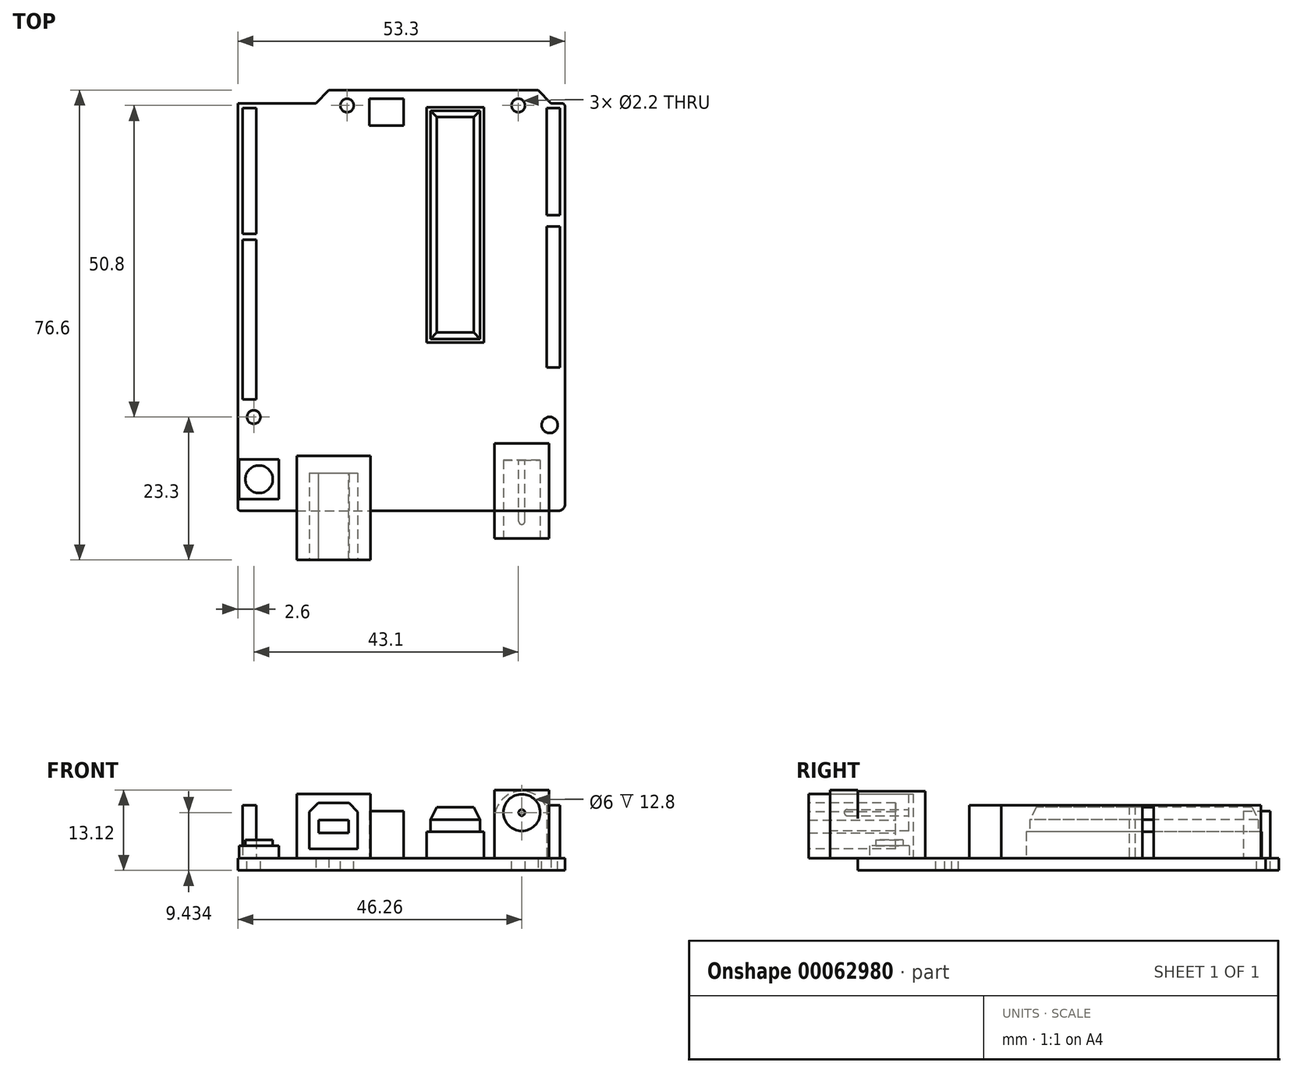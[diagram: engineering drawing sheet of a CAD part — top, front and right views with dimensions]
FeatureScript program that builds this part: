
annotation { "Feature Type Name" : "Feature", "Feature Type Description" : "" }
export const myFeature = defineFeature(function(context is Context, id is Id, definition is map)
    precondition{}
    {
        {
            var Q0;
            Q0=qCreatedBy(makeId("Top.planeOp"),FACE);
            var sketch = newSketch(context, id + "F0", { "sketchPlane" : qUnion([Q0])});
            skLineSegment(sketch, "E0.rect.bottom", {"start": v(-11.81, 34.3) * mm, "end": v(22.25, 34.3) * mm});
            skLineSegment(sketch, "E0.rect.top", {"start": v(-26.11, -34.3) * mm, "end": v(25.53, -34.3) * mm});
            skLineSegment(sketch, "E0.rect.left", {"start": v(-26.65, 32.16) * mm, "end": v(-26.65, -33.76) * mm});
            skLineSegment(sketch, "E0.rect.right", {"start": v(26.65, 31.62) * mm, "end": v(26.65, -33.18) * mm});
            skPoint(sketch, "E0.rect.middle", {"position": v(0, 0) * mm});
            skLineSegment(sketch, "E1.top", {"start": v(-25.49, 32.16) * mm, "end": v(-13.95, 32.16) * mm});
            skPoint(sketch, "E2.orphan", {"position": v(-26.65, 34.3) * mm});
            skLineSegment(sketch, "E3", {"start": v(-26.65, 32.16) * mm, "end": v(-25.49, 32.16) * mm});
            skLineSegment(sketch, "E4", {"start": v(-11.81, 34.3) * mm, "end": v(-13.95, 32.16) * mm});
            skLineSegment(sketch, "E5.top", {"start": v(24.39, 32.16) * mm, "end": v(26.11, 32.16) * mm});
            skLineSegment(sketch, "E6", {"start": v(22.25, 34.3) * mm, "end": v(24.39, 32.16) * mm});
            skPoint(sketch, "E7.orphan", {"position": v(26.65, 34.3) * mm});
            skPoint(sketch, "E8.visualSharp", {"position": v(26.65, -34.3) * mm});
            skArc(sketch, "E8.filletArc", {"start": v(25.53, -34.3) * mm, "mid": v(26.32, -33.97) * mm, "end": v(26.65, -33.18) * mm});
            skPoint(sketch, "E9.visualSharp", {"position": v(26.65, 32.16) * mm});
            skArc(sketch, "E9.filletArc", {"start": v(26.65, 31.62) * mm, "mid": v(26.5, 32) * mm, "end": v(26.11, 32.16) * mm});
            skPoint(sketch, "E10.visualSharp", {"position": v(-26.65, -34.3) * mm});
            skArc(sketch, "E10.filletArc", {"start": v(-26.65, -33.76) * mm, "mid": v(-26.5, -34.14) * mm, "end": v(-26.11, -34.3) * mm});
            skPoint(sketch, "E11.second.point", {"position": v(21.12, -10.57) * mm});
            skPoint(sketch, "E11.third.point", {"position": v(22.07, -8.93) * mm});
            skLineSegment(sketch, "E12", {"start": v(-13.95, 32.16) * mm, "end": v(31.22, 32.16) * mm, "construction": true});
            skSolve(sketch);
        }
        {
            var Q0;
            Q0=makeQuery(id+"F0.imprint","IMPRINT",FACE,{"disambiguationData":[TD([[makeQuery(id+"F0.imprint","IMPRINT",EDGE,{"derivedFrom":sQuery(id+"F0.wireOp",EDGE,"E0.rect.bottom")}),-1.0]])]});
            extrude(context, id + "F1", {"entities" : qUnion([Q0]), "depth" : 1.69 * mm});
        }
        {
            var Q0;
            Q0=makeQuery(id+"F1.opExtrude","CAP_FACE",FACE,{"disambiguationData":[OSD([sQuery(id+"F0.wireOp",EDGE,"E0.rect.bottom"),sQuery(id+"F0.wireOp",EDGE,"E0.rect.top"),sQuery(id+"F0.wireOp",EDGE,"E0.rect.left"),sQuery(id+"F0.wireOp",EDGE,"E0.rect.right"),sQuery(id+"F0.wireOp",EDGE,"E1.top"),sQuery(id+"F0.wireOp",EDGE,"E3"),sQuery(id+"F0.wireOp",EDGE,"E4"),sQuery(id+"F0.wireOp",EDGE,"E5.top"),sQuery(id+"F0.wireOp",EDGE,"E6"),sQuery(id+"F0.wireOp",EDGE,"E8.filletArc"),sQuery(id+"F0.wireOp",EDGE,"E9.filletArc"),sQuery(id+"F0.wireOp",EDGE,"E10.filletArc")])],"isStart":false});
            var sketch = newSketch(context, id + "F2", { "sketchPlane" : qUnion([Q0])});
            skLineSegment(sketch, "E13.top", {"start": v(23.65, -10.91) * mm, "end": v(25.85, -10.91) * mm});
            skLineSegment(sketch, "E13.left", {"start": v(23.65, 31.36) * mm, "end": v(23.65, 13.89) * mm});
            skLineSegment(sketch, "E13.right", {"start": v(25.85, 31.36) * mm, "end": v(25.85, 13.89) * mm});
            skLineSegment(sketch, "E14", {"start": v(23.65, 31.36) * mm, "end": v(25.85, 31.36) * mm});
            skLineSegment(sketch, "E15", {"start": v(23.65, 13.89) * mm, "end": v(25.85, 13.89) * mm});
            skLineSegment(sketch, "E16", {"start": v(23.65, 12.09) * mm, "end": v(25.85, 12.09) * mm});
            skLineSegment(sketch, "E17.trimOffspring", {"start": v(23.65, 12.09) * mm, "end": v(23.65, -10.91) * mm});
            skLineSegment(sketch, "E18.trimOffspring", {"start": v(25.85, 12.09) * mm, "end": v(25.85, -10.91) * mm});
            skLineSegment(sketch, "E19.bottom", {"start": v(-25.85, 31.36) * mm, "end": v(-23.65, 31.36) * mm});
            skLineSegment(sketch, "E19.top", {"start": v(-25.85, -16.12) * mm, "end": v(-23.65, -16.12) * mm});
            skLineSegment(sketch, "E19.left", {"start": v(-25.85, 31.36) * mm, "end": v(-25.85, 10.88) * mm});
            skLineSegment(sketch, "E19.right", {"start": v(-23.65, 31.36) * mm, "end": v(-23.65, 10.88) * mm});
            skLineSegment(sketch, "E20.bottom", {"start": v(-25.85, 10.88) * mm, "end": v(-23.65, 10.88) * mm});
            skLineSegment(sketch, "E20.top", {"start": v(-25.85, 9.88) * mm, "end": v(-23.65, 9.88) * mm});
            skLineSegment(sketch, "E21.trimOffspring", {"start": v(-23.65, 9.88) * mm, "end": v(-23.65, -16.12) * mm});
            skLineSegment(sketch, "E22.trimOffspring", {"start": v(-25.85, 9.88) * mm, "end": v(-25.85, -16.12) * mm});
            skSolve(sketch);
        }
        {
            var Q0;
            Q0=makeQuery(id+"F2.imprint","IMPRINT",FACE,{"disambiguationData":[TD([[makeQuery(id+"F2.imprint","IMPRINT",EDGE,{"derivedFrom":sQuery(id+"F2.wireOp",EDGE,"E13.top")}),1.0]])]});
            var Q1;
            Q1=makeQuery(id+"F2.imprint","IMPRINT",FACE,{"disambiguationData":[TD([[makeQuery(id+"F2.imprint","IMPRINT",EDGE,{"derivedFrom":sQuery(id+"F2.wireOp",EDGE,"E13.left")}),1.0]])]});
            var Q2;
            Q2=makeQuery(id+"F2.imprint","IMPRINT",FACE,{"disambiguationData":[TD([[makeQuery(id+"F2.imprint","IMPRINT",EDGE,{"derivedFrom":sQuery(id+"F2.wireOp",EDGE,"E19.bottom")}),-1.0]])]});
            var Q3;
            Q3=makeQuery(id+"F2.imprint","IMPRINT",FACE,{"disambiguationData":[TD([[makeQuery(id+"F2.imprint","IMPRINT",EDGE,{"derivedFrom":sQuery(id+"F2.wireOp",EDGE,"E19.top")}),1.0]])]});
            extrude(context, id + "F3", {"entities" : qUnion([Q0, Q1, Q2, Q3]), "depth" : 8.6 * mm});
        }
        {
            var Q0;
            Q0=makeQuery(id+"F1.opExtrude","SWEPT_FACE",FACE,{"disambiguationData":[OSD([sQuery(id+"F0.wireOp",EDGE,"E0.rect.top")])]});
            cPlane(context, id + "F4", {"entities" : qUnion([Q0]), "cplaneType" : CPlaneType.OFFSET, "offset" : 0 * mm, "width" : 150 * mm, "height" : 150 * mm});
        }
        {
            var Q0;
            Q0=qCreatedBy(id+"F4.planeOp",FACE);
            var sketch = newSketch(context, id + "F5", { "sketchPlane" : qUnion([Q0])});
            skLineSegment(sketch, "E23", {"start": v(32.01, 1.68) * mm, "end": v(24.05, 1.68) * mm, "construction": true});
            skLineSegment(sketch, "E24.bottom", {"start": v(24.05, 1.68) * mm, "end": v(15.17, 1.68) * mm});
            skLineSegment(sketch, "E24.left", {"start": v(24.05, 1.68) * mm, "end": v(24.05, 8.18) * mm});
            skLineSegment(sketch, "E24.right", {"start": v(15.17, 1.68) * mm, "end": v(15.17, 8.18) * mm});
            skArc(sketch, "E25", {"start": v(24.05, 8.18) * mm, "mid": v(19.6, 12.62) * mm, "end": v(15.17, 8.18) * mm});
            skSolve(sketch);
        }
        {
            var Q0;
            Q0=makeQuery(id+"F5.imprint","IMPRINT",FACE,{"disambiguationData":[TD([[makeQuery(id+"F5.imprint","IMPRINT",EDGE,{"derivedFrom":sQuery(id+"F5.wireOp",EDGE,"E24.bottom")}),-1.0]])]});
            extrude(context, id + "F6", {"entities" : qUnion([Q0]), "oppositeDirection" : true, "depth" : 11 * mm});
        }
        {
            var Q0;
            Q0=qCreatedBy(id+"F4.planeOp",FACE);
            var sketch = newSketch(context, id + "F7", { "sketchPlane" : qUnion([Q0])});
            skLineSegment(sketch, "E26.bottom", {"start": v(15.17, 1.69) * mm, "end": v(24.05, 1.69) * mm});
            skLineSegment(sketch, "E26.top", {"start": v(15.17, 12.81) * mm, "end": v(24.05, 12.81) * mm});
            skLineSegment(sketch, "E26.left", {"start": v(15.17, 1.69) * mm, "end": v(15.17, 12.81) * mm});
            skLineSegment(sketch, "E26.right", {"start": v(24.05, 1.69) * mm, "end": v(24.05, 12.81) * mm});
            skSolve(sketch);
        }
        {
            var Q0;
            Q0=makeQuery(id+"F7.imprint","IMPRINT",FACE,{"disambiguationData":[TD([[makeQuery(id+"F7.imprint","IMPRINT",EDGE,{"derivedFrom":sQuery(id+"F7.wireOp",EDGE,"E26.bottom")}),1.0]])]});
            extrude(context, id + "F8", {"entities" : qUnion([Q0]), "operationType" : NewBodyOperationType.ADD, "depth" : 4.5 * mm});
        }
        {
            var Q0;
            Q0=makeQuery(id+"F8.opExtrude","CAP_FACE",FACE,{"disambiguationData":[OSD([sQuery(id+"F7.wireOp",EDGE,"E26.bottom"),sQuery(id+"F7.wireOp",EDGE,"E26.top"),sQuery(id+"F7.wireOp",EDGE,"E26.left"),sQuery(id+"F7.wireOp",EDGE,"E26.right")])],"isStart":false});
            var sketch = newSketch(context, id + "F9", { "sketchPlane" : qUnion([Q0])});
            skCircle(sketch, "E27", {"center": v(19.6, 9.12) * mm, "radius": 3 * mm});
            skSolve(sketch);
        }
        {
            var Q0;
            Q0=makeQuery(id+"F9.imprint","IMPRINT",FACE,{"disambiguationData":[TD([[makeQuery(id+"F9.imprint","IMPRINT",EDGE,{"derivedFrom":sQuery(id+"F9.wireOp",EDGE,"E27")}),1.0]])]});
            var Q1;
            Q1=sQuery(id+"F9.wireOp",EDGE,"E27");
            extrude(context, id + "F10", {"entities" : qUnion([Q0]), "operationType" : NewBodyOperationType.REMOVE, "surfaceEntities" : qUnion([Q1]), "oppositeDirection" : true, "depth" : 12.8 * mm});
        }
        {
            var Q0;
            Q0=makeQuery(id+"F10.boolean.opBoolean","COPY",FACE,{"derivedFrom":makeQuery(id+"F10.opExtrude","CAP_FACE",FACE,{"disambiguationData":[OSD([sQuery(id+"F9.wireOp",EDGE,"E27")])],"isStart":false})});
            var sketch = newSketch(context, id + "F11", { "sketchPlane" : qUnion([Q0])});
            skCircle(sketch, "E28.0", {"center": v(19.6, 9.12) * mm, "radius": 3 * mm});
            skCircle(sketch, "E29", {"center": v(19.6, 9.12) * mm, "radius": 0.5 * mm});
            skSolve(sketch);
        }
        {
            var Q0;
            Q0=makeQuery(id+"F11.imprint","IMPRINT",FACE,{"disambiguationData":[TD([[makeQuery(id+"F11.imprint","IMPRINT",EDGE,{"derivedFrom":sQuery(id+"F11.wireOp",EDGE,"E29")}),1.0]])]});
            var Q1;
            Q1=sQuery(id+"F11.wireOp",EDGE,"E29");
            extrude(context, id + "F12", {"entities" : qUnion([Q0]), "surfaceEntities" : qUnion([Q1]), "depth" : 10 * mm});
        }
        {
            var Q0;
            Q0=makeQuery(id+"F1.opExtrude","CAP_FACE",FACE,{"disambiguationData":[OSD([sQuery(id+"F0.wireOp",EDGE,"E0.rect.bottom"),sQuery(id+"F0.wireOp",EDGE,"E0.rect.top"),sQuery(id+"F0.wireOp",EDGE,"E0.rect.left"),sQuery(id+"F0.wireOp",EDGE,"E0.rect.right"),sQuery(id+"F0.wireOp",EDGE,"E1.top"),sQuery(id+"F0.wireOp",EDGE,"E3"),sQuery(id+"F0.wireOp",EDGE,"E4"),sQuery(id+"F0.wireOp",EDGE,"E5.top"),sQuery(id+"F0.wireOp",EDGE,"E6"),sQuery(id+"F0.wireOp",EDGE,"E8.filletArc"),sQuery(id+"F0.wireOp",EDGE,"E9.filletArc"),sQuery(id+"F0.wireOp",EDGE,"E10.filletArc")])],"isStart":false});
            var sketch = newSketch(context, id + "F13", { "sketchPlane" : qUnion([Q0])});
            skLineSegment(sketch, "E30.bottom", {"start": v(-17.05, -34.3) * mm, "end": v(-5.05, -34.3) * mm});
            skLineSegment(sketch, "E30.top", {"start": v(-17.05, -25.3) * mm, "end": v(-5.05, -25.3) * mm});
            skLineSegment(sketch, "E30.left", {"start": v(-17.05, -34.3) * mm, "end": v(-17.05, -25.3) * mm});
            skLineSegment(sketch, "E30.right", {"start": v(-5.05, -34.3) * mm, "end": v(-5.05, -25.3) * mm});
            skSolve(sketch);
        }
        {
            var Q0;
            Q0=makeQuery(id+"F13.imprint","IMPRINT",FACE,{"disambiguationData":[TD([[makeQuery(id+"F13.imprint","IMPRINT",EDGE,{"derivedFrom":sQuery(id+"F13.wireOp",EDGE,"E30.bottom")}),1.0]])]});
            extrude(context, id + "F14", {"entities" : qUnion([Q0]), "depth" : 10.5 * mm});
        }
        {
            var Q0;
            Q0=makeQuery(id+"F14.opExtrude","SWEPT_FACE",FACE,{"disambiguationData":[OSD([sQuery(id+"F13.wireOp",EDGE,"E30.bottom")])]});
            var sketch = newSketch(context, id + "F15", { "sketchPlane" : qUnion([Q0])});
            skLineSegment(sketch, "E31.bottom", {"start": v(-17.05, 12.2) * mm, "end": v(-5.05, 12.2) * mm});
            skLineSegment(sketch, "E31.top", {"start": v(-17.05, 1.69) * mm, "end": v(-5.05, 1.69) * mm});
            skLineSegment(sketch, "E31.left", {"start": v(-17.05, 12.2) * mm, "end": v(-17.05, 1.69) * mm});
            skLineSegment(sketch, "E31.right", {"start": v(-5.05, 12.2) * mm, "end": v(-5.05, 1.69) * mm});
            skSolve(sketch);
        }
        {
            var Q0;
            Q0=makeQuery(id+"F15.imprint","IMPRINT",FACE,{"disambiguationData":[TD([[makeQuery(id+"F15.imprint","IMPRINT",EDGE,{"derivedFrom":sQuery(id+"F15.wireOp",EDGE,"E31.bottom")}),-1.0]])]});
            extrude(context, id + "F16", {"entities" : qUnion([Q0]), "operationType" : NewBodyOperationType.ADD, "depth" : 8 * mm});
        }
        {
            var Q0;
            Q0=makeQuery(id+"F16.opExtrude","CAP_FACE",FACE,{"disambiguationData":[OSD([sQuery(id+"F15.wireOp",EDGE,"E31.bottom"),sQuery(id+"F15.wireOp",EDGE,"E31.top"),sQuery(id+"F15.wireOp",EDGE,"E31.left"),sQuery(id+"F15.wireOp",EDGE,"E31.right")])],"isStart":false});
            var sketch = newSketch(context, id + "F17", { "sketchPlane" : qUnion([Q0])});
            skLineSegment(sketch, "E32.rect.bottom", {"start": v(-15, 3.2) * mm, "end": v(-7.1, 3.2) * mm});
            skLineSegment(sketch, "E32.rect.top", {"start": v(-13.56, 10.7) * mm, "end": v(-8.54, 10.7) * mm});
            skLineSegment(sketch, "E32.rect.left", {"start": v(-15, 3.2) * mm, "end": v(-15, 9.25) * mm});
            skLineSegment(sketch, "E32.rect.right", {"start": v(-7.1, 3.2) * mm, "end": v(-7.1, 9.25) * mm});
            skPoint(sketch, "E32.rect.middle", {"position": v(-11.05, 6.94) * mm});
            skPoint(sketch, "E32.rect.middle.positionSnap0", {"position": v(-17.05, 6.94) * mm});
            skPoint(sketch, "E32.rect.middle.positionSnap1", {"position": v(-11.05, 12.2) * mm});
            skPoint(sketch, "E32.rect.centerSnap0", {"position": v(-17.05, 6.94) * mm});
            skPoint(sketch, "E32.rect.centerSnap1", {"position": v(-11.05, 12.2) * mm});
            skLineSegment(sketch, "E33", {"start": v(-15, 9.25) * mm, "end": v(-13.56, 10.7) * mm});
            skLineSegment(sketch, "E34", {"start": v(-8.54, 10.7) * mm, "end": v(-7.1, 9.25) * mm});
            skPoint(sketch, "E35.orphan", {"position": v(-15, 10.7) * mm});
            skPoint(sketch, "E36.orphan", {"position": v(-7.1, 10.7) * mm});
            skSolve(sketch);
        }
        {
            var Q0;
            Q0=makeQuery(id+"F17.imprint","IMPRINT",FACE,{"disambiguationData":[TD([[makeQuery(id+"F17.imprint","IMPRINT",EDGE,{"derivedFrom":sQuery(id+"F17.wireOp",EDGE,"E32.rect.bottom")}),1.0]])]});
            extrude(context, id + "F18", {"entities" : qUnion([Q0]), "operationType" : NewBodyOperationType.REMOVE, "oppositeDirection" : true, "depth" : 14.14 * mm});
        }
        {
            var Q0;
            Q0=makeQuery(id+"F18.boolean.opBoolean","COPY",FACE,{"derivedFrom":makeQuery(id+"F18.opExtrude","CAP_FACE",FACE,{"disambiguationData":[OSD([sQuery(id+"F17.wireOp",EDGE,"E32.rect.bottom"),sQuery(id+"F17.wireOp",EDGE,"E32.rect.top"),sQuery(id+"F17.wireOp",EDGE,"E32.rect.left"),sQuery(id+"F17.wireOp",EDGE,"E32.rect.right"),sQuery(id+"F17.wireOp",EDGE,"E33"),sQuery(id+"F17.wireOp",EDGE,"E34")])],"isStart":false})});
            var sketch = newSketch(context, id + "F19", { "sketchPlane" : qUnion([Q0])});
            skLineSegment(sketch, "E37.rect.bottom", {"start": v(-13.49, 5.84) * mm, "end": v(-8.6, 5.84) * mm});
            skLineSegment(sketch, "E37.rect.top", {"start": v(-13.49, 7.92) * mm, "end": v(-8.6, 7.92) * mm});
            skLineSegment(sketch, "E37.rect.left", {"start": v(-13.49, 5.84) * mm, "end": v(-13.49, 7.92) * mm});
            skLineSegment(sketch, "E37.rect.right", {"start": v(-8.6, 5.84) * mm, "end": v(-8.6, 7.92) * mm});
            skPoint(sketch, "E37.rect.middle", {"position": v(-11.05, 6.88) * mm});
            skPoint(sketch, "E37.rect.middle.positionSnap0", {"position": v(-11.05, 10.7) * mm});
            skPoint(sketch, "E37.rect.centerSnap0", {"position": v(-11.05, 10.7) * mm});
            skSolve(sketch);
        }
        {
            var Q0;
            Q0=qSketchRegion(id+"F19",true);
            var Q1;
            Q1=makeQuery(id+"F16.opExtrude","CAP_FACE",FACE,{"disambiguationData":[OSD([sQuery(id+"F15.wireOp",EDGE,"E31.bottom"),sQuery(id+"F15.wireOp",EDGE,"E31.top"),sQuery(id+"F15.wireOp",EDGE,"E31.left"),sQuery(id+"F15.wireOp",EDGE,"E31.right")])],"isStart":false});
            extrude(context, id + "F20", {"entities" : qUnion([Q0]), "endBound" : BoundingType.UP_TO_SURFACE, "endBoundEntityFace" : qUnion([Q1]), "depth" : 25 * mm});
        }
        {
            var Q0;
            Q0=makeQuery(id+"F1.opExtrude","CAP_FACE",FACE,{"disambiguationData":[OSD([sQuery(id+"F0.wireOp",EDGE,"E0.rect.bottom"),sQuery(id+"F0.wireOp",EDGE,"E0.rect.top"),sQuery(id+"F0.wireOp",EDGE,"E0.rect.left"),sQuery(id+"F0.wireOp",EDGE,"E0.rect.right"),sQuery(id+"F0.wireOp",EDGE,"E1.top"),sQuery(id+"F0.wireOp",EDGE,"E3"),sQuery(id+"F0.wireOp",EDGE,"E4"),sQuery(id+"F0.wireOp",EDGE,"E5.top"),sQuery(id+"F0.wireOp",EDGE,"E6"),sQuery(id+"F0.wireOp",EDGE,"E8.filletArc"),sQuery(id+"F0.wireOp",EDGE,"E9.filletArc"),sQuery(id+"F0.wireOp",EDGE,"E10.filletArc")])],"isStart":false});
            var sketch = newSketch(context, id + "F21", { "sketchPlane" : qUnion([Q0])});
            skLineSegment(sketch, "E38.rect.bottom", {"start": v(-26.44, -25.9) * mm, "end": v(-19.94, -25.9) * mm});
            skLineSegment(sketch, "E38.rect.top", {"start": v(-26.44, -32.4) * mm, "end": v(-19.94, -32.4) * mm});
            skLineSegment(sketch, "E38.rect.left", {"start": v(-26.44, -25.9) * mm, "end": v(-26.44, -32.4) * mm});
            skLineSegment(sketch, "E38.rect.right", {"start": v(-19.94, -25.9) * mm, "end": v(-19.94, -32.4) * mm});
            skPoint(sketch, "E38.rect.middle", {"position": v(-23.19, -29.14) * mm});
            skSolve(sketch);
        }
        {
            var Q0;
            Q0=makeQuery(id+"F21.imprint","IMPRINT",FACE,{"disambiguationData":[TD([[makeQuery(id+"F21.imprint","IMPRINT",EDGE,{"derivedFrom":sQuery(id+"F21.wireOp",EDGE,"E38.rect.bottom")}),-1.0]])]});
            extrude(context, id + "F22", {"entities" : qUnion([Q0]), "depth" : 2 * mm});
        }
        {
            var Q0;
            Q0=makeQuery(id+"F22.opExtrude","CAP_FACE",FACE,{"disambiguationData":[OSD([sQuery(id+"F21.wireOp",EDGE,"E38.rect.bottom"),sQuery(id+"F21.wireOp",EDGE,"E38.rect.top"),sQuery(id+"F21.wireOp",EDGE,"E38.rect.left"),sQuery(id+"F21.wireOp",EDGE,"E38.rect.right")])],"isStart":false});
            var sketch = newSketch(context, id + "F23", { "sketchPlane" : qUnion([Q0])});
            skCircle(sketch, "E39", {"center": v(-23.19, -29.14) * mm, "radius": 2.24 * mm});
            skPoint(sketch, "E39.centerSnap0", {"position": v(-26.44, -29.14) * mm});
            skSolve(sketch);
        }
        {
            var Q0;
            Q0=makeQuery(id+"F23.imprint","IMPRINT",FACE,{"disambiguationData":[TD([[makeQuery(id+"F23.imprint","IMPRINT",EDGE,{"derivedFrom":sQuery(id+"F23.wireOp",EDGE,"E39")}),1.0]])]});
            extrude(context, id + "F24", {"entities" : qUnion([Q0]), "depth" : 1 * mm});
        }
        {
            var Q0;
            Q0=makeQuery(id+"F1.opExtrude","CAP_FACE",FACE,{"disambiguationData":[OSD([sQuery(id+"F0.wireOp",EDGE,"E0.rect.bottom"),sQuery(id+"F0.wireOp",EDGE,"E0.rect.top"),sQuery(id+"F0.wireOp",EDGE,"E0.rect.left"),sQuery(id+"F0.wireOp",EDGE,"E0.rect.right"),sQuery(id+"F0.wireOp",EDGE,"E1.top"),sQuery(id+"F0.wireOp",EDGE,"E3"),sQuery(id+"F0.wireOp",EDGE,"E4"),sQuery(id+"F0.wireOp",EDGE,"E5.top"),sQuery(id+"F0.wireOp",EDGE,"E6"),sQuery(id+"F0.wireOp",EDGE,"E8.filletArc"),sQuery(id+"F0.wireOp",EDGE,"E9.filletArc"),sQuery(id+"F0.wireOp",EDGE,"E10.filletArc")])],"isStart":false});
            var sketch = newSketch(context, id + "F25", { "sketchPlane" : qUnion([Q0])});
            skLineSegment(sketch, "E40.bottom", {"start": v(13.47, 31.5) * mm, "end": v(4.14, 31.5) * mm});
            skLineSegment(sketch, "E40.top", {"start": v(13.47, -6.87) * mm, "end": v(4.14, -6.87) * mm});
            skLineSegment(sketch, "E40.left", {"start": v(13.47, 31.5) * mm, "end": v(13.47, -6.87) * mm});
            skLineSegment(sketch, "E40.right", {"start": v(4.14, 31.5) * mm, "end": v(4.14, -6.87) * mm});
            skSolve(sketch);
        }
        {
            var Q0;
            Q0=makeQuery(id+"F25.imprint","IMPRINT",FACE,{"disambiguationData":[TD([[makeQuery(id+"F25.imprint","IMPRINT",EDGE,{"derivedFrom":sQuery(id+"F25.wireOp",EDGE,"E40.bottom")}),1.0]])]});
            extrude(context, id + "F26", {"entities" : qUnion([Q0]), "depth" : 4.3 * mm});
        }
        {
            var Q0;
            Q0=makeQuery(id+"F26.opExtrude","CAP_FACE",FACE,{"disambiguationData":[OSD([sQuery(id+"F25.wireOp",EDGE,"E40.bottom"),sQuery(id+"F25.wireOp",EDGE,"E40.top"),sQuery(id+"F25.wireOp",EDGE,"E40.left"),sQuery(id+"F25.wireOp",EDGE,"E40.right")])],"isStart":false});
            var sketch = newSketch(context, id + "F27", { "sketchPlane" : qUnion([Q0])});
            skLineSegment(sketch, "E41.rect.bottom", {"start": v(4.76, 30.91) * mm, "end": v(12.84, 30.91) * mm});
            skLineSegment(sketch, "E41.rect.top", {"start": v(4.76, -6.28) * mm, "end": v(12.84, -6.28) * mm});
            skLineSegment(sketch, "E41.rect.left", {"start": v(4.76, 30.91) * mm, "end": v(4.76, -6.28) * mm});
            skLineSegment(sketch, "E41.rect.right", {"start": v(12.84, 30.91) * mm, "end": v(12.84, -6.28) * mm});
            skPoint(sketch, "E41.rect.middle", {"position": v(8.8, 12.32) * mm});
            skPoint(sketch, "E41.rect.middle.positionSnap0", {"position": v(8.8, 31.5) * mm});
            skPoint(sketch, "E41.rect.middle.positionSnap1", {"position": v(4.14, 12.32) * mm});
            skPoint(sketch, "E41.rect.centerSnap0", {"position": v(8.8, 31.5) * mm});
            skPoint(sketch, "E41.rect.centerSnap1", {"position": v(4.14, 12.32) * mm});
            skSolve(sketch);
        }
        {
            var Q0;
            Q0=makeQuery(id+"F27.imprint","IMPRINT",FACE,{"disambiguationData":[TD([[makeQuery(id+"F27.imprint","IMPRINT",EDGE,{"derivedFrom":sQuery(id+"F27.wireOp",EDGE,"E41.rect.bottom")}),-1.0]])]});
            extrude(context, id + "F28", {"entities" : qUnion([Q0]), "depth" : 2 * mm});
        }
        {
            var Q0;
            Q0=makeQuery(id+"F28.opExtrude","CAP_FACE",FACE,{"disambiguationData":[OSD([sQuery(id+"F27.wireOp",EDGE,"E41.rect.bottom"),sQuery(id+"F27.wireOp",EDGE,"E41.rect.top"),sQuery(id+"F27.wireOp",EDGE,"E41.rect.left"),sQuery(id+"F27.wireOp",EDGE,"E41.rect.right")])],"isStart":false});
            cPlane(context, id + "F29", {"entities" : qUnion([Q0]), "cplaneType" : CPlaneType.OFFSET, "offset" : 2 * mm, "width" : 150 * mm, "height" : 150 * mm});
        }
        {
            var Q0;
            Q0=qCreatedBy(id+"F29.planeOp",FACE);
            var sketch = newSketch(context, id + "F30", { "sketchPlane" : qUnion([Q0])});
            skLineSegment(sketch, "E42.bottom", {"start": v(5.78, 29.94) * mm, "end": v(11.83, 29.94) * mm});
            skLineSegment(sketch, "E42.top", {"start": v(5.78, -5.22) * mm, "end": v(11.83, -5.22) * mm});
            skLineSegment(sketch, "E42.left", {"start": v(5.78, 29.94) * mm, "end": v(5.78, -5.22) * mm});
            skLineSegment(sketch, "E42.right", {"start": v(11.83, 29.94) * mm, "end": v(11.83, -5.22) * mm});
            skSolve(sketch);
        }
        {
            var Q1;
            Q1=makeQuery(id+"F30.imprint","IMPRINT",FACE,{"disambiguationData":[TD([[makeQuery(id+"F30.imprint","IMPRINT",EDGE,{"derivedFrom":sQuery(id+"F30.wireOp",EDGE,"E42.bottom")}),-1.0]])]});
            var Q2;
            Q2=makeQuery(id+"F28.opExtrude","CAP_FACE",FACE,{"disambiguationData":[OSD([sQuery(id+"F27.wireOp",EDGE,"E41.rect.bottom"),sQuery(id+"F27.wireOp",EDGE,"E41.rect.top"),sQuery(id+"F27.wireOp",EDGE,"E41.rect.left"),sQuery(id+"F27.wireOp",EDGE,"E41.rect.right")])],"isStart":false});
            loft(context, id + "F31", {"sheetProfilesArray" : [{ "sheetProfileEntities" : qUnion([Q1]) }, { "sheetProfileEntities" : qUnion([Q2]) }]});
        }
        {
            var Q0;
            Q0=makeQuery(id+"F1.opExtrude","CAP_FACE",FACE,{"disambiguationData":[OSD([sQuery(id+"F0.wireOp",EDGE,"E0.rect.bottom"),sQuery(id+"F0.wireOp",EDGE,"E0.rect.top"),sQuery(id+"F0.wireOp",EDGE,"E0.rect.left"),sQuery(id+"F0.wireOp",EDGE,"E0.rect.right"),sQuery(id+"F0.wireOp",EDGE,"E1.top"),sQuery(id+"F0.wireOp",EDGE,"E3"),sQuery(id+"F0.wireOp",EDGE,"E4"),sQuery(id+"F0.wireOp",EDGE,"E5.top"),sQuery(id+"F0.wireOp",EDGE,"E6"),sQuery(id+"F0.wireOp",EDGE,"E8.filletArc"),sQuery(id+"F0.wireOp",EDGE,"E9.filletArc"),sQuery(id+"F0.wireOp",EDGE,"E10.filletArc")])],"isStart":false});
            var sketch = newSketch(context, id + "F32", { "sketchPlane" : qUnion([Q0])});
            skCircle(sketch, "E43", {"center": v(24.15, -20.3) * mm, "radius": 1.31 * mm});
            skLineSegment(sketch, "E44", {"start": v(24.15, -20.3) * mm, "end": v(-35.14, -20.3) * mm, "construction": true});
            skLineSegment(sketch, "E45.0", {"start": v(24.15, -19) * mm, "end": v(-35.14, -19) * mm, "construction": true});
            skCircle(sketch, "E46", {"center": v(-24.05, -19) * mm, "radius": 1.1 * mm});
            skSolve(sketch);
        }
        {
            var Q0;
            Q0=makeQuery(id+"F32.imprint","IMPRINT",FACE,{"disambiguationData":[TD([[makeQuery(id+"F32.imprint","IMPRINT",EDGE,{"derivedFrom":sQuery(id+"F32.wireOp",EDGE,"E46")}),1.0]])]});
            var Q1;
            Q1=makeQuery(id+"F32.imprint","IMPRINT",FACE,{"disambiguationData":[TD([[makeQuery(id+"F32.imprint","IMPRINT",EDGE,{"derivedFrom":sQuery(id+"F32.wireOp",EDGE,"E43")}),1.0]])]});
            var Q2;
            Q2=sQuery(id+"F32.wireOp",EDGE,"07041a57-2a46-4494-bb32-0d5364b2cb77");
            var Q3;
            Q3=sQuery(id+"F32.wireOp",EDGE,"E43");
            extrude(context, id + "F33", {"entities" : qUnion([Q0, Q1]), "operationType" : NewBodyOperationType.REMOVE, "surfaceEntities" : qUnion([Q2, Q3]), "endBound" : BoundingType.THROUGH_ALL, "oppositeDirection" : true, "depth" : 25 * mm});
        }
        {
            var Q0;
            Q0=makeQuery(id+"F12.opExtrude","CAP_FACE",FACE,{"disambiguationData":[OSD([sQuery(id+"F11.wireOp",EDGE,"E29")])],"isStart":false});
            var sketch = newSketch(context, id + "F34", { "sketchPlane" : qUnion([Q0])});
            skArc(sketch, "E47.0", {"start": v(19.6, 9.62) * mm, "mid": v(19.1, 9.12) * mm, "end": v(19.6, 8.62) * mm});
            skLineSegment(sketch, "E48", {"start": v(19.6, 9.62) * mm, "end": v(19.6, 8.62) * mm});
            skSolve(sketch);
        }
        {
            var Q0;
            {var subQ2=sQuery(id+"F34.wireOp",EDGE,"E48");Q0=makeQuery(id+"F34.imprint","IMPRINT",FACE,{"disambiguationData":[TD([[makeQuery(id+"F34.imprint","IMPRINT",EDGE,{"derivedFrom":subQ2}),1.0]])]});}
            var Q1;
            Q1=sQuery(id+"F34.wireOp",EDGE,"E48");
            revolve(context, id + "F35", {"operationType" : NewBodyOperationType.ADD, "entities" : qUnion([Q0]), "axis" : qUnion([Q1]), "revolveType" : RevolveType.ONE_DIRECTION, "angle" : 180 * degree});
        }
        {
            var Q0;
            Q0=makeQuery(id+"F1.opExtrude","CAP_FACE",FACE,{"disambiguationData":[OSD([sQuery(id+"F0.wireOp",EDGE,"E0.rect.bottom"),sQuery(id+"F0.wireOp",EDGE,"E0.rect.top"),sQuery(id+"F0.wireOp",EDGE,"E0.rect.left"),sQuery(id+"F0.wireOp",EDGE,"E0.rect.right"),sQuery(id+"F0.wireOp",EDGE,"E1.top"),sQuery(id+"F0.wireOp",EDGE,"E3"),sQuery(id+"F0.wireOp",EDGE,"E4"),sQuery(id+"F0.wireOp",EDGE,"E5.top"),sQuery(id+"F0.wireOp",EDGE,"E6"),sQuery(id+"F0.wireOp",EDGE,"E8.filletArc"),sQuery(id+"F0.wireOp",EDGE,"E9.filletArc"),sQuery(id+"F0.wireOp",EDGE,"E10.filletArc")])],"isStart":false});
            var sketch = newSketch(context, id + "F36", { "sketchPlane" : qUnion([Q0])});
            skCircle(sketch, "E49", {"center": v(-8.85, 31.8) * mm, "radius": 1.1 * mm});
            skCircle(sketch, "E50", {"center": v(19.05, 31.8) * mm, "radius": 1.1 * mm});
            skCircle(sketch, "E51.0", {"center": v(24.15, -20.3) * mm, "radius": 1.31 * mm, "construction": true});
            skCircle(sketch, "E52.0", {"center": v(-24.05, -19) * mm, "radius": 1.1 * mm});
            skSolve(sketch);
        }
        {
            var Q0;
            Q0 = qSketchRegion(id + "F36", true);
            extrude(context, id + "F37", {"entities" : qUnion([Q0]), "operationType" : NewBodyOperationType.REMOVE, "oppositeDirection" : true, "depth" : 25 * mm});
        }
        {
            var Q0;
            Q0=makeQuery(id+"F1.opExtrude","CAP_FACE",FACE,{"disambiguationData":[OSD([sQuery(id+"F0.wireOp",EDGE,"E0.rect.bottom"),sQuery(id+"F0.wireOp",EDGE,"E0.rect.top"),sQuery(id+"F0.wireOp",EDGE,"E0.rect.left"),sQuery(id+"F0.wireOp",EDGE,"E0.rect.right"),sQuery(id+"F0.wireOp",EDGE,"E1.top"),sQuery(id+"F0.wireOp",EDGE,"E3"),sQuery(id+"F0.wireOp",EDGE,"E4"),sQuery(id+"F0.wireOp",EDGE,"E5.top"),sQuery(id+"F0.wireOp",EDGE,"E6"),sQuery(id+"F0.wireOp",EDGE,"E8.filletArc"),sQuery(id+"F0.wireOp",EDGE,"E9.filletArc"),sQuery(id+"F0.wireOp",EDGE,"E10.filletArc")])],"isStart":false});
            var sketch = newSketch(context, id + "F38", { "sketchPlane" : qUnion([Q0])});
            skLineSegment(sketch, "E53.0", {"start": v(26.65, 31.62) * mm, "end": v(26.65, -33.18) * mm});
            skLineSegment(sketch, "E54.0", {"start": v(-26.11, -34.3) * mm, "end": v(25.53, -34.3) * mm});
            skLineSegment(sketch, "E55.0", {"start": v(-26.65, 32.16) * mm, "end": v(-26.65, -33.76) * mm});
            skLineSegment(sketch, "E56.0", {"start": v(-26.65, 32.16) * mm, "end": v(-13.95, 32.16) * mm});
            skLineSegment(sketch, "E57.0", {"start": v(-11.81, 34.3) * mm, "end": v(22.25, 34.3) * mm});
            skCircle(sketch, "E58.0", {"center": v(19.05, 31.8) * mm, "radius": 1.1 * mm});
            skCircle(sketch, "E59.0", {"center": v(-8.85, 31.8) * mm, "radius": 1.1 * mm});
            skCircle(sketch, "E60.0", {"center": v(-24.05, -19) * mm, "radius": 1.1 * mm});
            skCircle(sketch, "E61.0", {"center": v(24.15, -20.3) * mm, "radius": 1.31 * mm});
            skLineSegment(sketch, "E62.0", {"start": v(-11.81, 34.3) * mm, "end": v(-13.95, 32.16) * mm});
            skLineSegment(sketch, "E63.0", {"start": v(22.25, 34.3) * mm, "end": v(24.39, 32.16) * mm});
            skLineSegment(sketch, "E64.0", {"start": v(24.39, 32.16) * mm, "end": v(26.11, 32.16) * mm});
            skArc(sketch, "E65.0", {"start": v(26.65, 31.62) * mm, "mid": v(26.5, 32) * mm, "end": v(26.11, 32.16) * mm});
            skArc(sketch, "E66.0", {"start": v(-26.65, -33.76) * mm, "mid": v(-26.5, -34.14) * mm, "end": v(-26.11, -34.3) * mm});
            skArc(sketch, "E67.0", {"start": v(25.53, -34.3) * mm, "mid": v(26.32, -33.97) * mm, "end": v(26.65, -33.18) * mm});
            skSolve(sketch);
        }
        {
            var Q0;
            Q0 = qSketchRegion(id + "F38", true);
            extrude(context, id + "F39", {"entities" : qUnion([Q0]), "oppositeDirection" : true, "depth" : 2 * mm});
        }
        {
            var Q0;
            Q0=makeQuery(id+"F39.opExtrude","CAP_FACE",FACE,{"disambiguationData":[OSD([sQuery(id+"F38.wireOp",EDGE,"E53.0"),sQuery(id+"F38.wireOp",EDGE,"E54.0"),sQuery(id+"F38.wireOp",EDGE,"E55.0"),sQuery(id+"F38.wireOp",EDGE,"E56.0"),sQuery(id+"F38.wireOp",EDGE,"E57.0"),sQuery(id+"F38.wireOp",EDGE,"E58.0"),sQuery(id+"F38.wireOp",EDGE,"E59.0"),sQuery(id+"F38.wireOp",EDGE,"E60.0"),sQuery(id+"F38.wireOp",EDGE,"E61.0"),sQuery(id+"F38.wireOp",EDGE,"E62.0"),sQuery(id+"F38.wireOp",EDGE,"E63.0"),sQuery(id+"F38.wireOp",EDGE,"E64.0"),sQuery(id+"F38.wireOp",EDGE,"E65.0"),sQuery(id+"F38.wireOp",EDGE,"E66.0"),sQuery(id+"F38.wireOp",EDGE,"E67.0")])],"isStart":true});
            var sketch = newSketch(context, id + "F40", { "sketchPlane" : qUnion([Q0])});
            skCircle(sketch, "E68.0", {"center": v(-8.85, 31.8) * mm, "radius": 1.1 * mm, "construction": true});
            skLineSegment(sketch, "E69.bottom", {"start": v(0.35, 28.5) * mm, "end": v(-5.25, 28.5) * mm});
            skLineSegment(sketch, "E69.top", {"start": v(0.35, 32.9) * mm, "end": v(-5.25, 32.9) * mm});
            skLineSegment(sketch, "E69.left", {"start": v(0.35, 28.5) * mm, "end": v(0.35, 32.9) * mm});
            skLineSegment(sketch, "E69.right", {"start": v(-5.25, 28.5) * mm, "end": v(-5.25, 32.9) * mm});
            skSolve(sketch);
        }
        {
            var Q0;
            Q0 = qSketchRegion(id + "F40", true);
            extrude(context, id + "F41", {"entities" : qUnion([Q0]), "operationType" : NewBodyOperationType.ADD, "depth" : 7.7 * mm});
        }
    });
